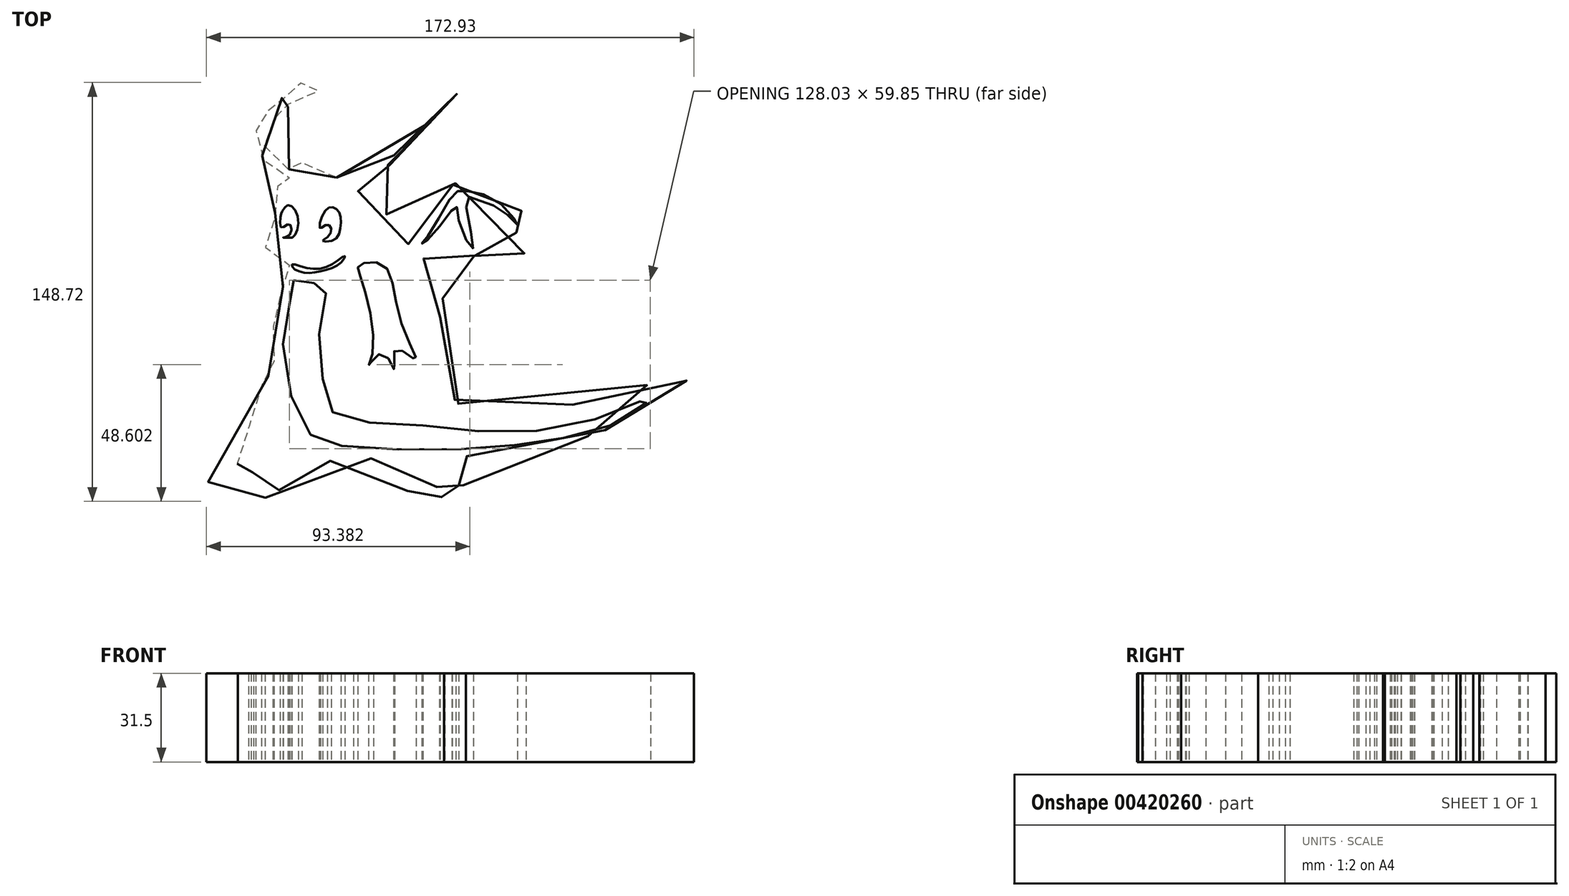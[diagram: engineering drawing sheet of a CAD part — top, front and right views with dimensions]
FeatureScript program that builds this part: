
annotation { "Feature Type Name" : "Feature", "Feature Type Description" : "" }
export const myFeature = defineFeature(function(context is Context, id is Id, definition is map)
    precondition{}
    {
        {
            var Q0;
            Q0=qCreatedBy(makeId("Top.planeOp"),FACE);
            var sketch = newSketch(context, id + "F0", { "sketchPlane" : qUnion([Q0])});
            skFitSpline(sketch, "E0", {"points": [v(8.84, 39.17) * mm, v(6.1, 41.3) * mm, v(0, 42.82) * mm, v(-3.35, 45.87) * mm, v(-3.66, 41) * mm, v(-7.62, 41.91) * mm, v(-14.63, 46.18) * mm, v(-16.46, 59.59) * mm, v(-8.53, 59.9) * mm, v(-7.62, 67.51) * mm, v(3.05, 70.26) * mm, v(0, 72.7) * mm, v(-8.23, 70.56) * mm, v(-10.97, 65.68) * mm, v(-11.58, 62.94) * mm, v(-17.37, 62.64) * mm, v(-19.81, 57.15) * mm, v(-17.98, 48.62) * mm, v(-13.72, 41.3) * mm, v(-7.01, 38.86) * mm, v(-10.36, 38.25) * mm, v(-12.8, 30.02) * mm, v(-14.02, 21.49) * mm, v(-16.15, 13.87) * mm, v(-8.23, 8.69) * mm, v(-9.14, 3.5) * mm, v(-12.8, -9.9) * mm, v(-13.72, -15.4) * mm, v(-13.41, -27.28) * mm, v(-14.94, -30.63) * mm, v(-22.25, -45.26) * mm, v(-23.16, -59.28) * mm, v(-37.19, -69.34) * mm, v(-20.73, -65.68) * mm, v(-26.21, -74.22) * mm, v(-11.58, -71.78) * mm, v(-3.66, -58.67) * mm, v(6.4, -61.42) * mm, v(31.09, -62.94) * mm, v(34.44, -73.6) * mm, v(39.32, -64.16) * mm, v(46.94, -75.44) * mm, v(45.72, -61.11) * mm, v(54.56, -73.91) * mm, v(51.2, -59.28) * mm, v(54.56, -59.59) * mm, v(98.15, -52.58) * mm, v(135.64, -34.3) * mm, v(124.97, -33.38) * mm, v(85.95, -42.82) * mm, v(51.51, -40.7) * mm, v(49.68, -27.28) * mm, v(45.72, -9.3) * mm, v(47.24, -5.64) * mm, v(39.62, 7.77) * mm, v(43.28, 13.56) * mm, v(54.25, 13.26) * mm, v(57.91, 11.43) * mm, v(58.83, 14.78) * mm, v(68.88, 21.8) * mm, v(72.85, 19.05) * mm, v(75.29, 12.04) * mm, v(75.29, 25.15) * mm, v(67.97, 32.16) * mm, v(51.82, 37.34) * mm, v(43.59, 26.37) * mm, v(35.05, 15.4) * mm, v(26.52, 26.06) * mm, v(17.07, 33.99) * mm, v(14.94, 36.12) * mm, v(18.9, 45.26) * mm, v(32.3, 43.74) * mm, v(52.12, 67.82) * mm, v(48.16, 67.82) * mm, v(32, 47.1) * mm, v(15.24, 51.36) * mm, v(8.84, 39.17) * mm]});
            skFitSpline(sketch, "E1", {"points": [v(-10.36, 27.28) * mm, v(-8.23, 29.41) * mm, v(-4.88, 24.84) * mm, v(-6.4, 18.14) * mm, v(-8.53, 17.83) * mm, v(-10.06, 17.83) * mm, v(-7.72, 18.95) * mm, v(-7.92, 22.6) * mm, v(-10.66, 21.38) * mm, v(-10.96, 25.53) * mm, v(-10.36, 27.28) * mm]});
            skFitSpline(sketch, "E2", {"points": [v(3.94, 16.72) * mm, v(7.88, 16.94) * mm, v(10.25, 21.56) * mm, v(9.8, 26.75) * mm, v(7.32, 28.67) * mm, v(4.16, 26.41) * mm, v(3.03, 21.11) * mm, v(5.4, 22.47) * mm, v(6.98, 20.55) * mm, v(4.95, 17.5) * mm, v(3.94, 16.72) * mm]});
            skFitSpline(sketch, "E3", {"points": [v(-6.96, 8.3) * mm, v(-1.5, 7) * mm, v(7.06, 8.3) * mm, v(11.73, 11.28) * mm, v(10.56, 9.07) * mm, v(4.6, 6.22) * mm, v(-2.15, 5.3) * mm, v(-6.44, 7) * mm, v(-6.96, 8.3) * mm]});
            skFitSpline(sketch, "E4", {"points": [v(-6.41, 2.72) * mm, v(-4.7, 1.12) * mm, v(4.98, 2.03) * mm, v(3.5, -7.16) * mm, v(3.81, -31.24) * mm, v(8.38, -44.96) * mm, v(33.07, -48.31) * mm, v(71.48, -51.36) * mm, v(110.5, -43.13) * mm, v(120.24, -38.86) * mm, v(111.27, -46.4) * mm, v(83.6, -54.25) * mm, v(50.71, -57.28) * mm, v(8.47, -55.76) * mm, v(-1.98, -50.14) * mm, v(-10.21, -21.49) * mm, v(-7.16, -2.6) * mm, v(-6.41, 2.72) * mm]});
            skFitSpline(sketch, "E5", {"points": [v(17.22, 4.11) * mm, v(21.8, -21.8) * mm, v(20.27, -27.58) * mm, v(25.15, -23.32) * mm, v(29.41, -29.1) * mm, v(29.72, -21.8) * mm, v(36.73, -25.45) * mm, v(31.55, -11.73) * mm, v(25.45, 8.08) * mm, v(16.92, 8.08) * mm, v(17.22, 4.11) * mm]});
            skFitSpline(sketch, "E6", {"points": [v(41.3, 18.45) * mm, v(50.55, 33.52) * mm, v(53.82, 34.42) * mm, v(65.61, 30.98) * mm, v(73.06, 22.44) * mm, v(67.25, 27.7) * mm, v(58.54, 31.34) * mm, v(54.9, 31.7) * mm, v(57.27, 14.1) * mm, v(52.37, 23.35) * mm, v(51.1, 28.98) * mm, v(43.1, 19) * mm, v(39.12, 15.73) * mm, v(41.3, 18.45) * mm]});
            skSolve(sketch);
        }
        {
            var Q0;
            Q0 = qSketchRegion(id + "F0", true);
            extrude(context, id + "F1", {"entities" : qUnion([Q0]), "depth" : 31.5 * mm});
        }
    });
